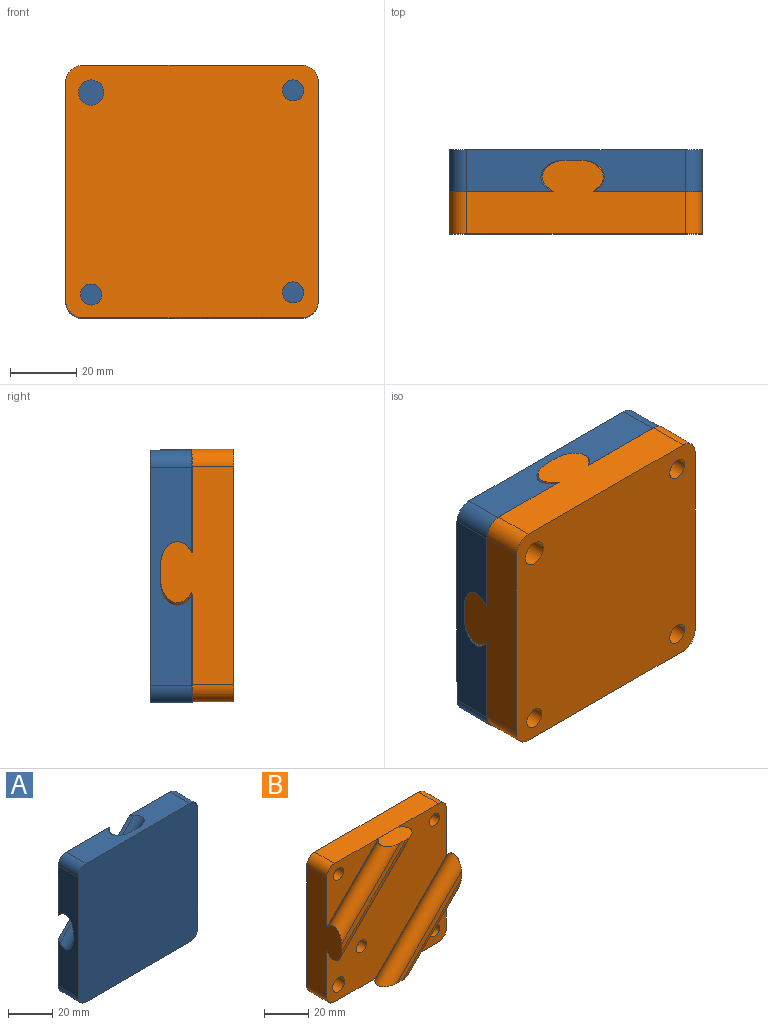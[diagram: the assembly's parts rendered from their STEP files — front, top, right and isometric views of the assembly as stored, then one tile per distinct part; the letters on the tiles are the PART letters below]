
ASSEMBLY  parts=2 mates=1
PART A: 217 faces, bbox 83.4x12.7x83.4 mm
  f0: plane 54.93x54.62mm, normal (0,1,0), area 1361.5mm2, adj f27,f28,f29,f30,f31,f32,f33,f34
  f1: plane 76.2x76.2mm, normal (0,1,0), area 2254mm2, adj f2,f3,f5,f7,f8,f9,f10,f19
  f2: plane 66.04x12.7mm, normal (0,0,-1), area 680.5mm2, adj f1,f4,f5,f14,f15,f18,f20,f22
  f3: plane 66.04x12.7mm, normal (1,0,0), area 680.5mm2, adj f1,f4,f5,f14,f15,f18,f19,f22
  f4: plane 41.48x41.48mm, normal (0,1,0), area 187.6mm2, adj f2,f3,f23,f24
  f5: plane 46.98x46.98mm, normal (0.54,-0.64,-0.54), area 102.9mm2, adj f1,f2,f3,f24
  f6: plane 41.48x41.48mm, normal (0,1,0), area 187.6mm2, adj f7,f8,f25,f26
  f7: plane 66.04x12.7mm, normal (0,0,1), area 680.5mm2, adj f1,f6,f9,f12,f13,f19,f21,f22
  f8: plane 66.04x12.7mm, normal (-1,0,0), area 680.5mm2, adj f1,f6,f9,f12,f13,f20,f21,f22
  f9: plane 46.98x46.98mm, normal (-0.54,-0.64,0.54), area 102.9mm2, adj f1,f7,f8,f26
  f10: cylinder r=3.3mm len=7.59mm, axis (0,1,0), area 157.6mm2, adj f1,f11
  f11: plane 6.6x6.6mm, normal (0,1,0), area 27mm2, adj f10,f16
  f12: plane 32.6x32.6mm, normal (0.54,-0.64,-0.54), area 70.9mm2, adj f7,f8,f13,f25
  f13: plane 32.6x32.6mm, normal (0,1,0), area 525.9mm2, adj f7,f8,f12,f21
  f14: plane 32.6x32.6mm, normal (-0.54,-0.64,0.54), area 70.9mm2, adj f2,f3,f15,f23
  f15: plane 32.6x32.6mm, normal (0,1,0), area 525.9mm2, adj f2,f3,f14,f18
  f16: cylinder r=1.52mm len=3.05mm, axis (0,1,0), area 9.3mm2, adj f11,f17
  f17: plane 3.05x3.05mm, normal (0,1,0), area 7.3mm2, adj f16
  f18: cylinder r=5.08mm len=12.7mm, axis (0,-1,0), area 101.3mm2, adj f2,f3,f15,f22
  f19: cylinder r=5.08mm len=12.7mm, axis (0,1,0), area 101.3mm2, adj f1,f3,f7,f22
  f20: cylinder r=5.08mm len=12.7mm, axis (0,1,0), area 101.3mm2, adj f1,f2,f8,f22
  f21: cylinder r=5.08mm len=12.7mm, axis (0,-1,0), area 101.3mm2, adj f7,f8,f13,f22
  f22: plane 76.2x76.2mm, normal (0,-1,0), area 5784.3mm2, adj f2,f3,f7,f8,f18,f19,f20,f21
  f23: cylinder r=5.08mm len=40.27mm, axis (-0.71,0,-0.71), area 513.1mm2, adj f2,f3,f4,f14
  f24: cylinder r=5.08mm len=52.26mm, axis (0.71,0,0.71), area 760.9mm2, adj f2,f3,f4,f5
  f25: cylinder r=5.08mm len=40.27mm, axis (-0.71,0,-0.71), area 513.1mm2, adj f6,f7,f8,f12
  f26: cylinder r=5.08mm len=52.26mm, axis (-0.71,0,-0.71), area 760.9mm2, adj f6,f7,f8,f9
  f27: plane 21.83x21.27mm, normal (-0.72,0,-0.7), area 271mm2, adj f0,f1,f28,f30
  f28: plane 33.66x32.79mm, normal (-0.7,0,0.72), area 417.7mm2, adj f0,f1,f27,f29
  f29: plane 21.83x21.27mm, normal (0.72,0,0.7), area 271mm2, adj f0,f1,f28,f30
  f30: plane 33.66x32.79mm, normal (0.7,0,-0.72), area 417.7mm2, adj f0,f1,f27,f29
  f31: plane 2.54x1.36mm, normal (-0.7,0,0.71), area 4.9mm2, adj f0,f32,f50,f51
  f32: plane 2.54x0.44mm, normal (0.71,0,0.7), area 1.6mm2, adj f0,f31,f33,f51
  f33: plane 2.54x0.86mm, normal (0.7,0,-0.71), area 3.1mm2, adj f0,f32,f34,f51
  f34: plane 2.54x1.17mm, normal (0.71,0,0.7), area 4.2mm2, adj f0,f33,f35,f51
  f35: extruded ~2.54x0.87mm, area 2.8mm2, adj f0,f34,f36,f51
  f36: extruded ~2.54x1.5mm, area 4.3mm2, adj f0,f35,f37,f51
  f37: extruded ~2.54x1.56mm, area 4.6mm2, adj f0,f36,f38,f51
  f38: extruded ~2.54x1.55mm, area 4.5mm2, adj f0,f37,f39,f51
  f39: extruded ~2.54x1.52mm, area 4.3mm2, adj f0,f38,f40,f51
  f40: extruded ~2.54x1.23mm, area 3.7mm2, adj f0,f39,f41,f51
  f41: plane 2.54x0.62mm, normal (-0.37,0,-0.93), area 1.7mm2, adj f0,f40,f42,f51
  f42: extruded ~2.54x1.4mm, area 4.3mm2, adj f0,f41,f43,f51
  f43: extruded ~2.54x1.33mm, area 4mm2, adj f0,f42,f44,f51
  f44: extruded ~2.54x1.4mm, area 3.6mm2, adj f0,f43,f45,f51
  f45: extruded ~2.54x1.31mm, area 4mm2, adj f0,f44,f46,f51
  f46: extruded ~2.54x1.98mm, area 5.7mm2, adj f0,f45,f47,f51
  f47: extruded ~2.54x1.91mm, area 5.5mm2, adj f0,f46,f48,f51
  f48: extruded ~2.54x0.8mm, area 2.7mm2, adj f0,f47,f49,f51
  f49: extruded ~2.54x0.78mm, area 2.3mm2, adj f0,f48,f50,f51
  f50: plane 2.54x1.93mm, normal (-0.71,0,-0.7), area 6.9mm2, adj f0,f31,f49,f51
  f51: plane 6.05x6.02mm, normal (0,1,0), area 9.9mm2, adj f31,f32,f33,f34,f35,f36,f37,f38
  f52: plane 2.54x0.48mm, normal (0.7,0,-0.71), area 1.7mm2, adj f0,f53,f55,f56
  f53: plane 4.19x4.16mm, normal (-0.71,0,-0.7), area 15mm2, adj f0,f52,f54,f56
  f54: plane 2.54x0.48mm, normal (-0.7,0,0.71), area 1.7mm2, adj f0,f53,f55,f56
  f55: plane 4.19x4.16mm, normal (0.71,0,0.7), area 15mm2, adj f0,f52,f54,f56
  f56: plane 4.67x4.64mm, normal (0,1,0), area 4mm2, adj f52,f53,f54,f55
  f57: extruded ~2.54x0.77mm, area 2.2mm2, adj f58,f76,f77,f78
  f58: extruded ~2.54x0.74mm, area 2.1mm2, adj f57,f59,f77,f78
  f59: extruded ~2.54x0.82mm, area 2.4mm2, adj f58,f60,f77,f78
  f60: plane 2.54x1.5mm, normal (-0.7,0,0.71), area 5.4mm2, adj f59,f76,f77,f78
  f61: extruded ~2.54x1.44mm, area 4.1mm2, adj f0,f62,f75,f77
  f62: extruded ~2.54x0.55mm, area 1.8mm2, adj f0,f61,f63,f77
  f63: extruded ~2.54x0.61mm, area 1.7mm2, adj f0,f62,f64,f77
  f64: plane 2.54x0.43mm, normal (-0.71,0,-0.7), area 1.5mm2, adj f0,f63,f65,f77
  f65: extruded ~2.54x0.66mm, area 1.9mm2, adj f0,f64,f66,f77
  f66: extruded ~2.54x0.49mm, area 1.6mm2, adj f0,f65,f67,f77
  f67: extruded ~2.54x0.94mm, area 2.7mm2, adj f0,f66,f68,f77
  f68: extruded ~2.54x1.02mm, area 2.9mm2, adj f0,f67,f69,f77
  f69: plane 2.54x2.02mm, normal (0.7,0,-0.71), area 7.2mm2, adj f0,f68,f70,f77
  f70: plane 2.54x0.29mm, normal (-0.71,0,-0.7), area 1.1mm2, adj f0,f69,f71,f77
  f71: extruded ~2.54x1.3mm, area 3.8mm2, adj f0,f70,f72,f77
  f72: extruded ~2.54x1.24mm, area 3.5mm2, adj f0,f71,f73,f77
  f73: extruded ~2.54x1.37mm, area 3.9mm2, adj f0,f72,f74,f77
  f74: extruded ~2.54x1.48mm, area 4.3mm2, adj f0,f73,f75,f77
  f75: extruded ~2.54x1.48mm, area 4.3mm2, adj f0,f61,f74,f77
  f76: extruded ~2.54x0.86mm, area 2.4mm2, adj f57,f60,f77,f78
  f77: plane 4.54x4.15mm, normal (0,1,0), area 7.3mm2, adj f57,f58,f59,f60,f61,f62,f63,f64
  f78: plane 1.97x1.9mm, normal (0,1,0), area 2mm2, adj f57,f58,f59,f60,f76
  f79: plane 2.54x1.89mm, normal (0.71,0,0.7), area 6.8mm2, adj f0,f80,f95,f96
  f80: plane 2.54x0.48mm, normal (0.7,0,-0.71), area 1.7mm2, adj f0,f79,f81,f96
  f81: plane 2.54x1.92mm, normal (-0.71,0,-0.7), area 6.9mm2, adj f0,f80,f82,f96
  f82: extruded ~2.54x1.08mm, area 3.2mm2, adj f0,f81,f83,f96
  f83: extruded ~2.54x1.07mm, area 3.1mm2, adj f0,f82,f84,f96
  f84: extruded ~2.54x0.67mm, area 2mm2, adj f0,f83,f85,f96
  f85: extruded ~2.54x0.72mm, area 1.9mm2, adj f0,f84,f86,f96
  f86: plane 2.54x0.03mm, normal (-0.7,0,0.71), area 0.1mm2, adj f0,f85,f87,f96
  f87: plane 2.54x0.48mm, normal (-0.82,0,-0.57), area 1.5mm2, adj f0,f86,f88,f96
  f88: plane 2.54x0.39mm, normal (-0.7,0,0.71), area 1.4mm2, adj f0,f87,f89,f96
  f89: plane 2.96x2.93mm, normal (0.71,0,0.7), area 10.6mm2, adj f0,f88,f90,f96
  f90: plane 2.54x0.48mm, normal (0.7,0,-0.71), area 1.7mm2, adj f0,f89,f91,f96
  f91: plane 2.54x1.53mm, normal (-0.71,0,-0.7), area 5.5mm2, adj f0,f90,f92,f96
  f92: extruded ~2.54x1.02mm, area 3.1mm2, adj f0,f91,f93,f96
  f93: extruded ~2.54x0.91mm, area 2.6mm2, adj f0,f92,f94,f96
  f94: extruded ~2.54x0.67mm, area 2mm2, adj f0,f93,f95,f96
  f95: extruded ~2.54x0.7mm, area 2.1mm2, adj f0,f79,f94,f96
  f96: plane 5.43x4.96mm, normal (0,1,0), area 6.7mm2, adj f79,f80,f81,f82,f83,f84,f85,f86
  f97: plane 2.54x1.89mm, normal (0.71,0,0.7), area 6.8mm2, adj f0,f98,f113,f114
  f98: plane 2.54x0.48mm, normal (0.7,0,-0.71), area 1.7mm2, adj f0,f97,f99,f114
  f99: plane 2.54x1.92mm, normal (-0.71,0,-0.7), area 6.9mm2, adj f0,f98,f100,f114
  f100: extruded ~2.54x1.08mm, area 3.2mm2, adj f0,f99,f101,f114
  f101: extruded ~2.54x1.07mm, area 3.1mm2, adj f0,f100,f102,f114
  f102: extruded ~2.54x0.67mm, area 2mm2, adj f0,f101,f103,f114
  f103: extruded ~2.54x0.72mm, area 1.9mm2, adj f0,f102,f104,f114
  f104: plane 2.54x0.03mm, normal (-0.7,0,0.71), area 0.1mm2, adj f0,f103,f105,f114
  f105: plane 2.54x0.48mm, normal (-0.82,0,-0.57), area 1.5mm2, adj f0,f104,f106,f114
  f106: plane 2.54x0.39mm, normal (-0.7,0,0.71), area 1.4mm2, adj f0,f105,f107,f114
  f107: plane 2.96x2.93mm, normal (0.71,0,0.7), area 10.6mm2, adj f0,f106,f108,f114
  f108: plane 2.54x0.48mm, normal (0.7,0,-0.71), area 1.7mm2, adj f0,f107,f109,f114
  f109: plane 2.54x1.53mm, normal (-0.71,0,-0.7), area 5.5mm2, adj f0,f108,f110,f114
  f110: extruded ~2.54x1.02mm, area 3.1mm2, adj f0,f109,f111,f114
  f111: extruded ~2.54x0.91mm, area 2.6mm2, adj f0,f110,f112,f114
  f112: extruded ~2.54x0.67mm, area 2mm2, adj f0,f111,f113,f114
  f113: extruded ~2.54x0.7mm, area 2.1mm2, adj f0,f97,f112,f114
  f114: plane 5.43x4.96mm, normal (0,1,0), area 6.7mm2, adj f97,f98,f99,f100,f101,f102,f103,f104
  f115: extruded ~2.54x1.18mm, area 3.3mm2, adj f0,f116,f140,f141
  f116: extruded ~2.54x0.57mm, area 1.7mm2, adj f0,f115,f117,f141
  f117: extruded ~2.54x0.67mm, area 1.7mm2, adj f0,f116,f118,f141
  f118: extruded ~2.54x0.96mm, area 2.6mm2, adj f0,f117,f119,f141
  f119: extruded ~2.54x0.77mm, area 2.1mm2, adj f0,f118,f120,f141
  f120: extruded ~2.54x0.48mm, area 1.2mm2, adj f0,f119,f121,f141
  f121: extruded ~2.54x0.4mm, area 1.2mm2, adj f0,f120,f122,f141
  f122: extruded ~2.54x0.62mm, area 1.7mm2, adj f0,f121,f123,f141
  f123: extruded ~2.54x0.7mm, area 2.1mm2, adj f0,f122,f124,f141
  f124: extruded ~2.54x1.15mm, area 3.5mm2, adj f0,f123,f125,f141
  f125: plane 2.54x0.58mm, normal (-0.43,0,-0.9), area 1.6mm2, adj f0,f124,f126,f141
  f126: extruded ~2.54x1.3mm, area 4mm2, adj f0,f125,f127,f141
  f127: extruded ~2.54x1.18mm, area 3.5mm2, adj f0,f126,f128,f141
  f128: extruded ~2.54x1.07mm, area 3mm2, adj f0,f127,f129,f141
  f129: extruded ~2.54x0.93mm, area 2.7mm2, adj f0,f128,f130,f141
  f130: extruded ~2.54x1.24mm, area 3.3mm2, adj f0,f129,f131,f141
  f131: extruded ~2.54x0.82mm, area 2.2mm2, adj f0,f130,f132,f141
  f132: extruded ~2.54x0.51mm, area 1.3mm2, adj f0,f131,f133,f141
  f133: extruded ~2.54x0.4mm, area 1.2mm2, adj f0,f132,f134,f141
  f134: extruded ~2.54x0.69mm, area 1.9mm2, adj f0,f133,f135,f141
  f135: extruded ~2.54x0.83mm, area 2.5mm2, adj f0,f134,f136,f141
  f136: extruded ~2.54x0.61mm, area 2mm2, adj f0,f135,f137,f141
  f137: extruded ~2.54x0.71mm, area 2.1mm2, adj f0,f136,f138,f141
  f138: plane 2.54x0.47mm, normal (0.71,0,0.7), area 1.7mm2, adj f0,f137,f139,f141
  f139: extruded ~2.54x1.26mm, area 4mm2, adj f0,f138,f140,f141
  f140: extruded ~2.54x1.33mm, area 3.9mm2, adj f0,f115,f139,f141
  f141: plane 6x5.3mm, normal (0,1,0), area 7.6mm2, adj f115,f116,f117,f118,f119,f120,f121,f122
  f142: plane 2.54x2.17mm, normal (0.88,0,0.47), area 6.2mm2, adj f0,f143,f167,f168
  f143: plane 2.54x0.57mm, normal (0.7,0,-0.71), area 2mm2, adj f0,f142,f144,f168
  f144: plane 3.75x2.54mm, normal (-0.5,0,-0.87), area 11mm2, adj f0,f143,f145,f168
  f145: plane 2.54x0.5mm, normal (-0.7,0,0.71), area 1.8mm2, adj f0,f144,f146,f168
  f146: plane 2.54x1.98mm, normal (0.51,0,0.86), area 5.8mm2, adj f0,f145,f147,f168
  f147: extruded ~2.54x1.07mm, area 3.2mm2, adj f0,f146,f148,f168
  f148: plane 2.54x0.02mm, normal (-0.7,0,0.71), area 0.1mm2, adj f0,f147,f149,f168
  f149: extruded ~2.54x0.21mm, area 0.6mm2, adj f0,f148,f150,f168
  f150: extruded ~2.54x0.25mm, area 0.7mm2, adj f0,f149,f151,f168
  f151: extruded ~2.54x0.27mm, area 0.8mm2, adj f0,f150,f152,f168
  f152: extruded ~2.54x0.26mm, area 0.7mm2, adj f0,f151,f153,f168
  f153: plane 2.54x2.17mm, normal (-0.88,0,-0.47), area 6.2mm2, adj f0,f152,f154,f168
  f154: plane 2.54x0.53mm, normal (-0.7,0,0.71), area 1.9mm2, adj f0,f153,f155,f168
  f155: plane 2.54x2.18mm, normal (0.46,0,0.89), area 6.3mm2, adj f0,f154,f156,f168
  f156: extruded ~2.54x0.78mm, area 2.3mm2, adj f0,f155,f157,f168
  f157: plane 2.54x0.2mm, normal (0.54,0,0.84), area 0.6mm2, adj f0,f156,f158,f168
  f158: plane 2.54x0.02mm, normal (-0.7,0,0.71), area 0.1mm2, adj f0,f157,f159,f168
  f159: extruded ~2.54x0.97mm, area 2.9mm2, adj f0,f158,f160,f168
  f160: extruded ~2.54x2.08mm, area 6.1mm2, adj f0,f159,f161,f168
  f161: plane 2.54x0.5mm, normal (-0.7,0,0.71), area 1.8mm2, adj f0,f160,f162,f168
  f162: plane 3.76x2.54mm, normal (0.87,0,0.49), area 11mm2, adj f0,f161,f163,f168
  f163: plane 2.54x0.55mm, normal (0.7,0,-0.71), area 2mm2, adj f0,f162,f164,f168
  f164: plane 2.54x2.18mm, normal (-0.46,0,-0.89), area 6.2mm2, adj f0,f163,f165,f168
  f165: extruded ~2.54x0.98mm, area 2.9mm2, adj f0,f164,f166,f168
  f166: plane 2.54x0.02mm, normal (0.7,0,-0.71), area 0.1mm2, adj f0,f165,f167,f168
  f167: extruded ~2.54x0.99mm, area 2.9mm2, adj f0,f142,f166,f168
  f168: plane 6.33x6.32mm, normal (0,1,0), area 10.1mm2, adj f142,f143,f144,f145,f146,f147,f148,f149
  f169: extruded ~2.54x0.86mm, area 2.5mm2, adj f170,f196,f197,f198
  f170: extruded ~2.54x0.52mm, area 1.5mm2, adj f169,f171,f197,f198
  f171: extruded ~2.54x0.5mm, area 1.4mm2, adj f170,f172,f197,f198
  f172: extruded ~2.54x0.68mm, area 1.9mm2, adj f171,f173,f197,f198
  f173: extruded ~2.54x0.9mm, area 2.7mm2, adj f172,f174,f197,f198
  f174: plane 2.54x0.46mm, normal (0.67,0,-0.74), area 1.6mm2, adj f173,f175,f197,f198
  f175: plane 2.54x0.27mm, normal (0.71,0,0.7), area 1mm2, adj f174,f196,f197,f198
  f176: plane 2.54x0.51mm, normal (0.85,0,0.53), area 1.5mm2, adj f0,f177,f195,f197
  f177: plane 2.54x0.35mm, normal (0.7,0,-0.71), area 1.3mm2, adj f0,f176,f178,f197
  f178: plane 2.54x2.01mm, normal (-0.71,0,-0.7), area 7.2mm2, adj f0,f177,f179,f197
  f179: extruded ~2.54x1.01mm, area 2.9mm2, adj f0,f178,f180,f197
  f180: extruded ~2.54x1.03mm, area 3mm2, adj f0,f179,f181,f197
  f181: extruded ~2.54x0.59mm, area 1.9mm2, adj f0,f180,f182,f197
  f182: extruded ~2.54x0.67mm, area 1.9mm2, adj f0,f181,f183,f197
  f183: plane 2.54x0.51mm, normal (0.92,0,0.38), area 1.4mm2, adj f0,f182,f184,f197
  f184: extruded ~2.54x0.55mm, area 1.5mm2, adj f0,f183,f185,f197
  f185: extruded ~2.54x0.51mm, area 1.6mm2, adj f0,f184,f186,f197
  f186: extruded ~2.54x0.62mm, area 1.8mm2, adj f0,f185,f187,f197
  f187: extruded ~2.54x0.64mm, area 1.9mm2, adj f0,f186,f188,f197
  f188: plane 2.54x0.18mm, normal (0.71,0,0.7), area 0.6mm2, adj f0,f187,f189,f197
  f189: plane 2.54x0.52mm, normal (-0.68,0,0.74), area 1.8mm2, adj f0,f188,f190,f197
  f190: extruded ~2.54x2.35mm, area 6.9mm2, adj f0,f189,f191,f197
  f191: extruded ~2.54x0.89mm, area 2.6mm2, adj f0,f190,f192,f197
  f192: extruded ~2.54x0.91mm, area 2.6mm2, adj f0,f191,f193,f197
  f193: extruded ~2.54x0.65mm, area 2mm2, adj f0,f192,f194,f197
  f194: extruded ~2.54x0.81mm, area 2.1mm2, adj f0,f193,f195,f197
  f195: plane 2.54x0.02mm, normal (0.7,0,-0.71), area 0.1mm2, adj f0,f176,f194,f197
  f196: extruded ~2.54x0.85mm, area 2.5mm2, adj f169,f175,f197,f198
  f197: plane 4.8x4.5mm, normal (0,1,0), area 7.2mm2, adj f169,f170,f171,f172,f173,f174,f175,f176
  f198: plane 2.27x1.72mm, normal (0,1,0), area 2.5mm2, adj f169,f170,f171,f172,f173,f174,f175,f196
  f199: plane 2.54x1.89mm, normal (0.71,0,0.7), area 6.8mm2, adj f0,f200,f215,f216
  f200: plane 2.54x0.48mm, normal (0.7,0,-0.71), area 1.7mm2, adj f0,f199,f201,f216
  f201: plane 2.54x1.92mm, normal (-0.71,0,-0.7), area 6.9mm2, adj f0,f200,f202,f216
  f202: extruded ~2.54x1.08mm, area 3.2mm2, adj f0,f201,f203,f216
  f203: extruded ~2.54x1.07mm, area 3.1mm2, adj f0,f202,f204,f216
  f204: extruded ~2.54x0.67mm, area 2mm2, adj f0,f203,f205,f216
  f205: extruded ~2.54x0.72mm, area 1.9mm2, adj f0,f204,f206,f216
  f206: plane 2.54x0.03mm, normal (-0.7,0,0.71), area 0.1mm2, adj f0,f205,f207,f216
  f207: plane 2.54x0.48mm, normal (-0.82,0,-0.57), area 1.5mm2, adj f0,f206,f208,f216
  f208: plane 2.54x0.39mm, normal (-0.7,0,0.71), area 1.4mm2, adj f0,f207,f209,f216
  f209: plane 2.96x2.93mm, normal (0.71,0,0.7), area 10.6mm2, adj f0,f208,f210,f216
  f210: plane 2.54x0.48mm, normal (0.7,0,-0.71), area 1.7mm2, adj f0,f209,f211,f216
  f211: plane 2.54x1.53mm, normal (-0.71,0,-0.7), area 5.5mm2, adj f0,f210,f212,f216
  f212: extruded ~2.54x1.02mm, area 3.1mm2, adj f0,f211,f213,f216
  f213: extruded ~2.54x0.91mm, area 2.6mm2, adj f0,f212,f214,f216
  f214: extruded ~2.54x0.67mm, area 2mm2, adj f0,f213,f215,f216
  f215: extruded ~2.54x0.7mm, area 2.1mm2, adj f0,f199,f214,f216
  f216: plane 5.43x4.96mm, normal (0,1,0), area 6.7mm2, adj f199,f200,f201,f202,f203,f204,f205,f206
PART B: 32 faces, bbox 83.4x22.2x83.4 mm
  f0: cylinder r=3.25mm len=6.5mm, axis (0,-1,0), area 90.8mm2, adj f7,f25
  f1: plane 76.2x76.19mm, normal (0,1,0), area 5642.8mm2, adj f2,f4,f12,f15,f17,f18,f19,f20
  f2: plane 66.03x22.2mm, normal (1,0,0), area 988.6mm2, adj f1,f3,f5,f6,f7,f16,f17,f19
  f3: plane 32.93x32.93mm, normal (0.54,0.64,-0.54), area 68.7mm2, adj f2,f4,f16,f21
  f4: plane 66.04x22.2mm, normal (0,0,-1), area 988.9mm2, adj f1,f3,f5,f6,f7,f16,f17,f18
  f5: plane 46.6x46.58mm, normal (-0.54,0.64,0.54), area 97.8mm2, adj f2,f4,f7,f22
  f6: plane 41.09x41.08mm, normal (0,-1,0), area 157.3mm2, adj f2,f4,f21,f22
  f7: plane 76.2x76.19mm, normal (0,-1,0), area 3639.6mm2, adj f0,f2,f4,f5,f11,f12,f15,f18
  f8: plane 12.43x0.01mm, normal (0,1,0), area 0.1mm2, adj f9,f10,f11,f15
  f9: plane 32.93x32.92mm, normal (-0.54,0.64,0.54), area 68.7mm2, adj f8,f10,f12,f14,f15,f24
  f10: plane 18.4x9.45mm, normal (0,0,1), area 149.6mm2, adj f8,f9,f11,f13,f23,f24
  f11: plane 46.6x46.58mm, normal (0.54,0.64,-0.54), area 97.8mm2, adj f7,f8,f10,f12,f15,f23
  f12: plane 66.03x22.2mm, normal (-1,0,0), area 988.6mm2, adj f1,f7,f9,f11,f13,f14,f18,f20
  f13: plane 41.09x41.08mm, normal (0,-1,0), area 157.3mm2, adj f10,f12,f23,f24
  f14: plane 32.92x32.92mm, normal (0,-1,0), area 504.5mm2, adj f9,f12,f15,f20,f29
  f15: plane 66.04x12.75mm, normal (0,0,1), area 839.3mm2, adj f1,f7,f8,f9,f11,f14,f19,f20
  f16: plane 32.93x32.93mm, normal (0,-1,0), area 504.9mm2, adj f2,f3,f4,f17,f28
  f17: cylinder r=5.08mm len=12.7mm, axis (0,1,0), area 101.3mm2, adj f1,f2,f4,f16
  f18: cylinder r=5.08mm len=12.7mm, axis (0,-1,0), area 101.3mm2, adj f1,f4,f7,f12
  f19: cylinder r=5.08mm len=12.7mm, axis (0,1,0), area 101.3mm2, adj f1,f2,f7,f15
  f20: cylinder r=5.08mm len=12.7mm, axis (0,-1,0), area 101.3mm2, adj f1,f12,f14,f15
  f21: cylinder r=5.08mm len=40.65mm, axis (-0.71,0,-0.71), area 519.3mm2, adj f2,f3,f4,f6
  f22: cylinder r=5.08mm len=51.88mm, axis (-0.71,0,-0.71), area 754.5mm2, adj f2,f4,f5,f6
  f23: cylinder r=5.08mm len=51.88mm, axis (-0.71,0,-0.71), area 754.5mm2, adj f10,f11,f12,f13
  f24: cylinder r=5.08mm len=40.65mm, axis (-0.71,0,-0.71), area 519.3mm2, adj f9,f10,f12,f13
  f25: plane 6.5x6.5mm, normal (0,-1,0), area 26.1mm2, adj f0,f26
  f26: cylinder r=1.5mm len=3mm, axis (0,-1,0), area 9.4mm2, adj f25,f27
  f27: plane 3x3mm, normal (0,-1,0), area 7.1mm2, adj f26
  f28: cylinder r=3.17mm len=12.7mm, axis (0,1,0), area 253.4mm2, adj f1,f16
  f29: cylinder r=3.17mm len=12.7mm, axis (0,1,0), area 253.4mm2, adj f1,f14
  f30: cylinder r=3.81mm len=12.7mm, axis (0,1,0), area 304mm2, adj f1,f7
  f31: cylinder r=3.17mm len=12.7mm, axis (0,1,0), area 253.4mm2, adj f1,f7
PLACE A rot(axis=(0,0,1),180deg) t=(-47.89,-13.13,-3.73)mm
PLACE B rot(axis=(-1,0,0),180deg) t=(2.96,-13,47.42)mm fixed
MATE slider A.f24 <-> B.f23  axis (-0.71,0,0.71) through (-64.48,-8.63,28.93)mm
